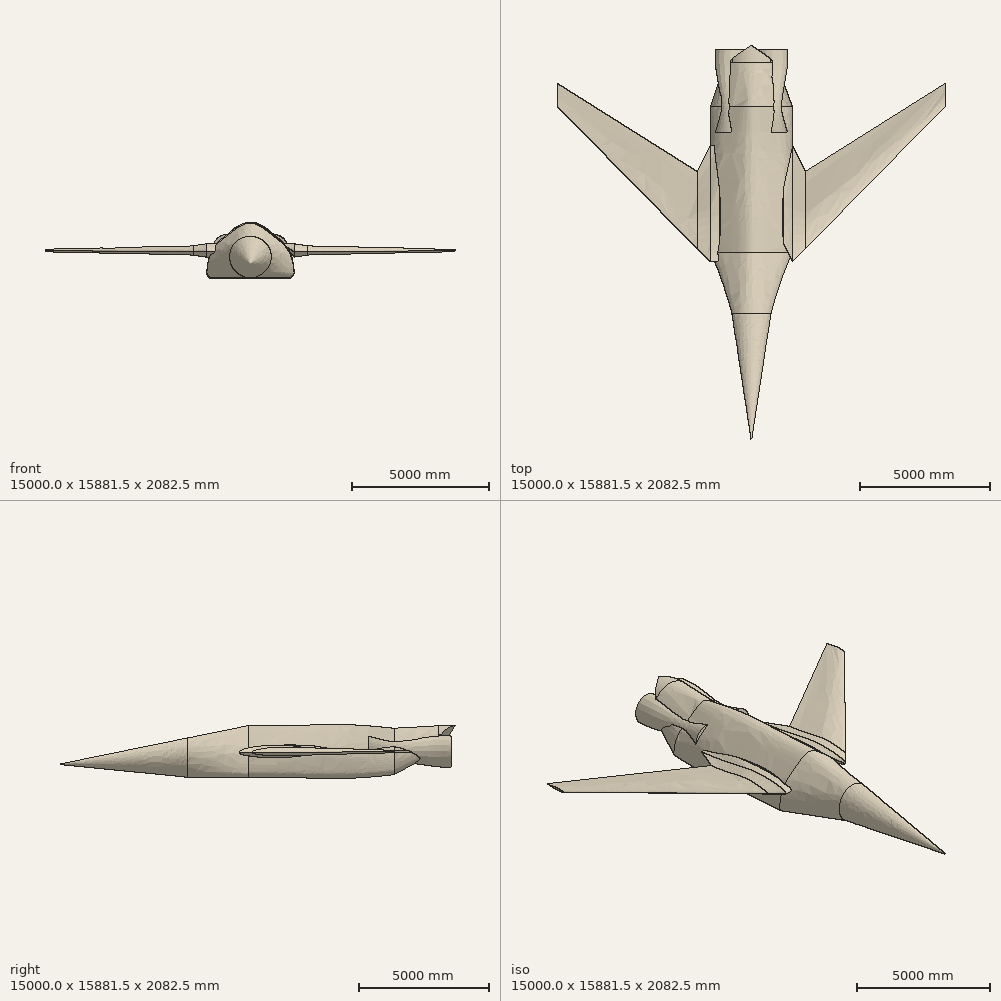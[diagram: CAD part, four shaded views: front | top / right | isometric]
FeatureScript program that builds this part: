
annotation { "Feature Type Name" : "Feature", "Feature Type Description" : "" }
export const myFeature = defineFeature(function(context is Context, id is Id, definition is map)
    precondition{}
    {
        {
            var Q0;
            Q0=qCreatedBy(makeId("Right.planeOp"),FACE);
            var sketch = newSketch(context, id + "F0", { "sketchPlane" : qUnion([Q0])});
            skLineSegment(sketch, "E0", {"start": v(0, 0) * mm, "end": v(-1750, 0) * mm});
            skLineSegment(sketch, "E1", {"start": v(-1750, 0) * mm, "end": v(-3500, 0) * mm});
            skLineSegment(sketch, "E2", {"start": v(-3500, 0) * mm, "end": v(-3500, -1000) * mm});
            skLineSegment(sketch, "E3", {"start": v(-3500, -1000) * mm, "end": v(-8500, -1000) * mm});
            skLineSegment(sketch, "E4", {"start": v(-8500, -1000) * mm, "end": v(-8500, -499.31) * mm});
            skLineSegment(sketch, "E5", {"start": v(-1151.4, 0) * mm, "end": v(-1151.4, 1000) * mm});
            skLineSegment(sketch, "E6", {"start": v(-1151.4, 1000) * mm, "end": v(-8500, -499.31) * mm});
            skLineSegment(sketch, "E7", {"start": v(-8500, -499.31) * mm, "end": v(-3500, -1000) * mm});
            skLineSegment(sketch, "E8", {"start": v(-3500, 0) * mm, "end": v(-3500, 520.82) * mm});
            skLineSegment(sketch, "E9", {"start": v(-8500, -499.31) * mm, "end": v(-8450, -499.31) * mm});
            skLineSegment(sketch, "E10", {"start": v(-8450, -499.31) * mm, "end": v(-8450, -489.1) * mm});
            skLineSegment(sketch, "E11", {"start": v(-8450, -499.31) * mm, "end": v(-8450, -504.32) * mm});
            skSolve(sketch);
        }
        {
            var Q0;
            Q0=sQuery(id+"F0.wireOp",EDGE,"E5");
            cPlane(context, id + "F1", {"entities" : qUnion([Q0]), "cplaneType" : CPlaneType.LINE_ANGLE, "offset" : 25 * mm, "angle" : 90 * degree, "oppositeDirection" : true, "width" : 150 * mm, "height" : 150 * mm});
        }
        {
            var Q0;
            Q0=qCreatedBy(id+"F1.planeOp",FACE);
            var sketch = newSketch(context, id + "F2", { "sketchPlane" : qUnion([Q0])});
            skLineSegment(sketch, "E12.top", {"start": v(-1394.2, -1000) * mm, "end": v(1394.2, -1000) * mm});
            skPoint(sketch, "E12.middle", {"position": v(0, 0) * mm});
            skFitSpline(sketch, "E13", {"points": [v(-1600, -1000) * mm, v(-848, 530) * mm, v(0, 1000) * mm, v(848, 530) * mm, v(1600, -1000) * mm], "startDerivative": vector(0, 10524.75) * mm, "endDerivative": vector(0, -10524.75) * mm});
            skArc(sketch, "E14", {"start": v(-735.27, 618.52) * mm, "mid": v(-1273.27, 435.52) * mm, "end": v(-1440.68, -107.53) * mm});
            skArc(sketch, "E15", {"start": v(1440.68, -107.53) * mm, "mid": v(1273.27, 435.52) * mm, "end": v(735.27, 618.52) * mm});
            skFitSpline(sketch, "E16.trimOffspring", {"points": [v(-1600, -1000) * mm, v(-848, 530) * mm, v(0, 1000) * mm, v(848, 530) * mm, v(1600, -1000) * mm], "startDerivative": vector(0, 10524.75) * mm, "endDerivative": vector(0, -10524.75) * mm});
            skFitSpline(sketch, "E17.trimOffspring", {"points": [v(-1600, -1000) * mm, v(-848, 530) * mm, v(0, 1000) * mm, v(848, 530) * mm, v(1600, -1000) * mm], "startDerivative": vector(0, 10524.75) * mm, "endDerivative": vector(0, -10524.75) * mm});
            skArc(sketch, "E18.filletArc", {"start": v(-1593.82, -787.83) * mm, "mid": v(-1539.85, -937.05) * mm, "end": v(-1394.2, -1000) * mm});
            skArc(sketch, "E19.filletArc", {"start": v(1394.2, -1000) * mm, "mid": v(1539.85, -937.05) * mm, "end": v(1593.82, -787.83) * mm});
            skSolve(sketch);
        }
        {
            var Q0;
            Q0=qCreatedBy(makeId("Front.planeOp"),FACE);
            var sketch = newSketch(context, id + "F3", { "sketchPlane" : qUnion([Q0])});
            skLineSegment(sketch, "E20.top", {"start": v(-1394.2, -1000) * mm, "end": v(1394.2, -1000) * mm});
            skPoint(sketch, "E20.middle", {"position": v(0, 0) * mm});
            skFitSpline(sketch, "E21", {"points": [v(-1600, -1000) * mm, v(-848, 530) * mm, v(0, 1000) * mm, v(848, 530) * mm, v(1600, -1000) * mm], "startDerivative": vector(0, 10524.75) * mm, "endDerivative": vector(0, -10524.75) * mm});
            skArc(sketch, "E22", {"start": v(-735.27, 618.52) * mm, "mid": v(-1273.27, 435.52) * mm, "end": v(-1440.68, -107.53) * mm});
            skArc(sketch, "E23", {"start": v(1440.68, -107.53) * mm, "mid": v(1273.27, 435.52) * mm, "end": v(735.27, 618.52) * mm});
            skFitSpline(sketch, "E24.trimOffspring", {"points": [v(-1600, -1000) * mm, v(-848, 530) * mm, v(0, 1000) * mm, v(848, 530) * mm, v(1600, -1000) * mm], "startDerivative": vector(0, 10524.75) * mm, "endDerivative": vector(0, -10524.75) * mm});
            skFitSpline(sketch, "E25.trimOffspring", {"points": [v(-1600, -1000) * mm, v(-848, 530) * mm, v(0, 1000) * mm, v(848, 530) * mm, v(1600, -1000) * mm], "startDerivative": vector(0, 10524.75) * mm, "endDerivative": vector(0, -10524.75) * mm});
            skArc(sketch, "E26.filletArc", {"start": v(-1593.82, -787.83) * mm, "mid": v(-1539.85, -937.05) * mm, "end": v(-1394.2, -1000) * mm});
            skArc(sketch, "E27.filletArc", {"start": v(1394.2, -1000) * mm, "mid": v(1539.85, -937.05) * mm, "end": v(1593.82, -787.83) * mm});
            skSolve(sketch);
        }
        {
            var Q0;
            Q0=qCreatedBy(makeId("Front.planeOp"),FACE);
            cPlane(context, id + "F4", {"entities" : qUnion([Q0]), "cplaneType" : CPlaneType.OFFSET, "offset" : 3500 * mm, "oppositeDirection" : true, "width" : 150 * mm, "height" : 150 * mm});
        }
        {
            var Q0;
            Q0=qCreatedBy(id+"F4.planeOp",FACE);
            var sketch = newSketch(context, id + "F5", { "sketchPlane" : qUnion([Q0])});
            skLineSegment(sketch, "E28.top", {"start": v(-1394.2, -1000) * mm, "end": v(1394.2, -1000) * mm});
            skPoint(sketch, "E28.middle", {"position": v(0, 0) * mm});
            skFitSpline(sketch, "E29", {"points": [v(-1600, -1000) * mm, v(-848, 530) * mm, v(0, 1000) * mm, v(848, 530) * mm, v(1600, -1000) * mm], "startDerivative": vector(0, 10524.75) * mm, "endDerivative": vector(0, -10524.75) * mm});
            skArc(sketch, "E30", {"start": v(-735.27, 618.52) * mm, "mid": v(-1273.27, 435.52) * mm, "end": v(-1440.68, -107.53) * mm});
            skArc(sketch, "E31", {"start": v(1440.68, -107.53) * mm, "mid": v(1273.27, 435.52) * mm, "end": v(735.27, 618.52) * mm});
            skFitSpline(sketch, "E32.trimOffspring", {"points": [v(-1600, -1000) * mm, v(-848, 530) * mm, v(0, 1000) * mm, v(848, 530) * mm, v(1600, -1000) * mm], "startDerivative": vector(0, 10524.75) * mm, "endDerivative": vector(0, -10524.75) * mm});
            skFitSpline(sketch, "E33.trimOffspring", {"points": [v(-1600, -1000) * mm, v(-848, 530) * mm, v(0, 1000) * mm, v(848, 530) * mm, v(1600, -1000) * mm], "startDerivative": vector(0, 10524.75) * mm, "endDerivative": vector(0, -10524.75) * mm});
            skArc(sketch, "E34.filletArc", {"start": v(-1593.82, -787.83) * mm, "mid": v(-1539.85, -937.05) * mm, "end": v(-1394.2, -1000) * mm});
            skArc(sketch, "E35.filletArc", {"start": v(1394.2, -1000) * mm, "mid": v(1539.85, -937.05) * mm, "end": v(1593.82, -787.83) * mm});
            skSolve(sketch);
        }
        {
            var Q0;
            Q0=qCreatedBy(makeId("Front.planeOp"),FACE);
            cPlane(context, id + "F6", {"entities" : qUnion([Q0]), "cplaneType" : CPlaneType.OFFSET, "offset" : 4500 * mm, "oppositeDirection" : true, "width" : 150 * mm, "height" : 150 * mm});
        }
        {
            var Q0;
            Q0=qCreatedBy(id+"F6.planeOp",FACE);
            var sketch = newSketch(context, id + "F7", { "sketchPlane" : qUnion([Q0])});
            skLineSegment(sketch, "E36.top", {"start": v(-1413.07, -900) * mm, "end": v(1413.07, -900) * mm});
            skPoint(sketch, "E36.middle", {"position": v(0, 0) * mm});
            skFitSpline(sketch, "E37", {"points": [v(-1600, -900) * mm, v(-784.42, 441.24) * mm, v(0, 900) * mm, v(784.42, 441.24) * mm, v(1600, -900) * mm], "startDerivative": vector(0, 9508.62) * mm, "endDerivative": vector(0, -9508.62) * mm});
            skArc(sketch, "E38", {"start": v(-719.25, 488.69) * mm, "mid": v(-1131.76, 394.84) * mm, "end": v(-1324.66, 18.33) * mm});
            skArc(sketch, "E39", {"start": v(1324.66, 18.33) * mm, "mid": v(1131.76, 394.84) * mm, "end": v(719.25, 488.69) * mm});
            skFitSpline(sketch, "E40.trimOffspring", {"points": [v(-1600, -900) * mm, v(-784.42, 441.24) * mm, v(0, 900) * mm, v(784.42, 441.24) * mm, v(1600, -900) * mm], "startDerivative": vector(0, 9508.62) * mm, "endDerivative": vector(0, -9508.62) * mm});
            skFitSpline(sketch, "E41.trimOffspring", {"points": [v(-1600, -900) * mm, v(-784.42, 441.24) * mm, v(0, 900) * mm, v(784.42, 441.24) * mm, v(1600, -900) * mm], "startDerivative": vector(0, 9508.62) * mm, "endDerivative": vector(0, -9508.62) * mm});
            skArc(sketch, "E42.filletArc", {"start": v(-1592.48, -705.43) * mm, "mid": v(-1545.4, -842.02) * mm, "end": v(-1413.07, -900) * mm});
            skArc(sketch, "E43.filletArc", {"start": v(1413.07, -900) * mm, "mid": v(1545.4, -842.02) * mm, "end": v(1592.48, -705.43) * mm});
            skLineSegment(sketch, "E44", {"start": v(-719.25, 488.69) * mm, "end": v(-1324.66, 18.33) * mm, "construction": true});
            skLineSegment(sketch, "E45", {"start": v(719.25, 488.69) * mm, "end": v(1324.66, 18.33) * mm, "construction": true});
            skSolve(sketch);
        }
        {
            var Q0;
            Q0=qCreatedBy(makeId("Front.planeOp"),FACE);
            cPlane(context, id + "F8", {"entities" : qUnion([Q0]), "cplaneType" : CPlaneType.OFFSET, "offset" : 6232.05 * mm, "oppositeDirection" : true, "width" : 150 * mm, "height" : 150 * mm});
        }
        {
            var Q0;
            Q0=qCreatedBy(id+"F8.planeOp",FACE);
            var sketch = newSketch(context, id + "F9", { "sketchPlane" : qUnion([Q0])});
            skArc(sketch, "E46", {"start": v(998.61, 52.63) * mm, "mid": v(0, 1000) * mm, "end": v(-998.61, 52.63) * mm});
            skLineSegment(sketch, "E47", {"start": v(0, 0) * mm, "end": v(-948.68, 0) * mm});
            skLineSegment(sketch, "E48", {"start": v(0, 0) * mm, "end": v(948.68, 0) * mm});
            skLineSegment(sketch, "E49", {"start": v(0, 1000) * mm, "end": v(0, 675) * mm, "construction": true});
            skLineSegment(sketch, "E50", {"start": v(0, 675) * mm, "end": v(-737.82, 675) * mm, "construction": true});
            skLineSegment(sketch, "E51", {"start": v(0, 675) * mm, "end": v(737.82, 675) * mm, "construction": true});
            skPoint(sketch, "E52.visualSharp", {"position": v(-1000, 0) * mm});
            skArc(sketch, "E52.filletArc", {"start": v(-998.61, 52.63) * mm, "mid": v(-984.96, 15.59) * mm, "end": v(-948.68, 0) * mm});
            skPoint(sketch, "E53.visualSharp", {"position": v(1000, 0) * mm});
            skArc(sketch, "E53.filletArc", {"start": v(948.68, 0) * mm, "mid": v(984.96, 15.59) * mm, "end": v(998.61, 52.63) * mm});
            skSolve(sketch);
        }
        {
            var Q0;
            Q0=makeQuery(id+"F2.imprint","IMPRINT",FACE,{"disambiguationData":[TD([[makeQuery(id+"F2.imprint","IMPRINT",EDGE,{"derivedFrom":sQuery(id+"F2.wireOp",EDGE,"E12.top")}),1.0]])]});
            var Q1;
            Q1=makeQuery(id+"F3.imprint","IMPRINT",FACE,{"disambiguationData":[TD([[makeQuery(id+"F3.imprint","IMPRINT",EDGE,{"derivedFrom":sQuery(id+"F3.wireOp",EDGE,"E20.top")}),1.0]])]});
            var Q2;
            Q2=makeQuery(id+"F5.imprint","IMPRINT",FACE,{"disambiguationData":[TD([[makeQuery(id+"F5.imprint","IMPRINT",EDGE,{"derivedFrom":sQuery(id+"F5.wireOp",EDGE,"E28.top")}),1.0]])]});
            var Q3;
            Q3=makeQuery(id+"F7.imprint","IMPRINT",FACE,{"disambiguationData":[TD([[makeQuery(id+"F7.imprint","IMPRINT",EDGE,{"derivedFrom":sQuery(id+"F7.wireOp",EDGE,"E36.top")}),1.0]])]});
            loft(context, id + "F10", {"sheetProfilesArray" : [{ "sheetProfileEntities" : qUnion([Q0]) }, { "sheetProfileEntities" : qUnion([Q1]) }, { "sheetProfileEntities" : qUnion([Q2]) }, { "sheetProfileEntities" : qUnion([Q3]) }]});
        }
        {
            var Q0;
            Q0=sQuery(id+"F7.wireOp",EDGE,"E44");
            var Q1;
            Q1=sQuery(id+"F9.wireOp",VERTEX,"E50.end");
            cPlane(context, id + "F11", {"entities" : qUnion([Q0, Q1]), "cplaneType" : CPlaneType.LINE_ANGLE, "offset" : 25 * mm, "angle" : 180 * degree, "width" : 150 * mm, "height" : 150 * mm});
        }
        {
            var Q0;
            Q0=qCreatedBy(id+"F11.planeOp",FACE);
            var sketch = newSketch(context, id + "F12", { "sketchPlane" : qUnion([Q0])});
            skLineSegment(sketch, "E54", {"start": v(-589.34, 4526.34) * mm, "end": v(-612.8, 6268.32) * mm});
            skLineSegment(sketch, "E55", {"start": v(-1354.08, 4472.19) * mm, "end": v(-612.8, 6268.32) * mm});
            skSolve(sketch);
        }
        {
            var Q0;
            Q0=sQuery(id+"F7.wireOp",EDGE,"E45");
            var Q1;
            Q1=sQuery(id+"F9.wireOp",VERTEX,"E51.end");
            cPlane(context, id + "F13", {"entities" : qUnion([Q0, Q1]), "cplaneType" : CPlaneType.LINE_ANGLE, "offset" : 25 * mm, "angle" : 0 * degree, "width" : 150 * mm, "height" : 150 * mm});
        }
        {
            var Q0;
            Q0=qCreatedBy(id+"F13.planeOp",FACE);
            var sketch = newSketch(context, id + "F14", { "sketchPlane" : qUnion([Q0])});
            skLineSegment(sketch, "E56", {"start": v(589.34, 4526.34) * mm, "end": v(612.8, 6268.32) * mm});
            skLineSegment(sketch, "E57", {"start": v(1354.08, 4472.19) * mm, "end": v(612.8, 6268.32) * mm});
            skSolve(sketch);
        }
        {
            var Q1;
            Q1=makeQuery(id+"F10.opLoft","CAP_FACE",FACE,{"disambiguationData":[OSD([makeQuery(id+"F7.imprint","IMPRINT",FACE,{"disambiguationData":[TD([[makeQuery(id+"F7.imprint","IMPRINT",EDGE,{"derivedFrom":sQuery(id+"F7.wireOp",EDGE,"E36.top")}),1.0]])]})])],"isStart":true});
            var Q2;
            Q2=makeQuery(id+"F9.imprint","IMPRINT",FACE,{"disambiguationData":[TD([[makeQuery(id+"F9.imprint","IMPRINT",EDGE,{"derivedFrom":sQuery(id+"F9.wireOp",EDGE,"E46")}),1.0]])]});
            var Q3;
            Q3=sQuery(id+"F12.wireOp",EDGE,"E54");
            var Q4;
            Q4=sQuery(id+"F14.wireOp",EDGE,"E56");
            loft(context, id + "F15", {"operationType" : NewBodyOperationType.ADD, "addGuides" : true, "sheetProfilesArray" : [{ "sheetProfileEntities" : qUnion([Q1]) }, { "sheetProfileEntities" : qUnion([Q2]) }], "guidesArray" : [{ "guideEntities" : qUnion([Q3]), "guideDerivativeType" : LoftGuideDerivativeType.DEFAULT, "guideDerivativeMagnitude" : 1 }, { "guideEntities" : qUnion([Q4]), "guideDerivativeType" : LoftGuideDerivativeType.DEFAULT, "guideDerivativeMagnitude" : 1 }]});
        }
        {
            var Q0;
            Q0=makeQuery(id+"F15.opLoft","CAP_FACE",FACE,{"disambiguationData":[OSD([makeQuery(id+"F9.imprint","IMPRINT",FACE,{"disambiguationData":[TD([[makeQuery(id+"F9.imprint","IMPRINT",EDGE,{"derivedFrom":sQuery(id+"F9.wireOp",EDGE,"E46")}),1.0]])]})])],"isStart":true});
            extrude(context, id + "F16", {"entities" : qUnion([Q0]), "operationType" : NewBodyOperationType.ADD, "depth" : 649.4 * mm, "offsetDistance" : 25 * mm});
        }
        {
            var Q0;
            Q0=qCreatedBy(makeId("Right.planeOp"),FACE);
            var sketch = newSketch(context, id + "F17", { "sketchPlane" : qUnion([Q0])});
            skLineSegment(sketch, "E58", {"start": v(0, 0) * mm, "end": v(4500, 0) * mm});
            skLineSegment(sketch, "E59", {"start": v(4500, 0) * mm, "end": v(6232.05, 0) * mm});
            skLineSegment(sketch, "E60", {"start": v(4500, 0) * mm, "end": v(4500, 1000) * mm});
            skLineSegment(sketch, "E61", {"start": v(4500, 1000) * mm, "end": v(6881.46, 1000) * mm});
            skLineSegment(sketch, "E62", {"start": v(6881.46, 1000) * mm, "end": v(6881.46, -1000) * mm});
            skLineSegment(sketch, "E63", {"start": v(6881.46, 1000) * mm, "end": v(6232.05, 0) * mm});
            skLineSegment(sketch, "E64", {"start": v(6232.05, 0) * mm, "end": v(5582.64, -1000) * mm});
            skLineSegment(sketch, "E65", {"start": v(5582.64, -1000) * mm, "end": v(6881.46, -1000) * mm});
            skSolve(sketch);
        }
        {
            var Q0;
            Q0=makeQuery(id+"F17.imprint","IMPRINT",FACE,{"disambiguationData":[TD([[makeQuery(id+"F17.imprint","IMPRINT",EDGE,{"derivedFrom":sQuery(id+"F17.wireOp",EDGE,"E62")}),-1.0]])]});
            var Q1;
            Q1=sQuery(id+"F17.wireOp",EDGE,"E61");
            revolve(context, id + "F18", {"operationType" : NewBodyOperationType.REMOVE, "entities" : qUnion([Q0]), "axis" : qUnion([Q1]), "revolveType" : RevolveType.SYMMETRIC, "oppositeDirection" : true, "angle" : 182 * degree});
        }
        {
            var Q0;
            Q0=qCreatedBy(id+"F1.planeOp",FACE);
            var sketch = newSketch(context, id + "F19", { "sketchPlane" : qUnion([Q0])});
            skLineSegment(sketch, "E66.top", {"start": v(-1394.2, -1000) * mm, "end": v(1394.2, -1000) * mm});
            skPoint(sketch, "E66.middle", {"position": v(0, 0) * mm});
            skFitSpline(sketch, "E67", {"points": [v(-1600, -1000) * mm, v(-848, 530) * mm, v(0, 1000) * mm, v(848, 530) * mm, v(1600, -1000) * mm], "startDerivative": vector(0, 10524.75) * mm, "endDerivative": vector(0, -10524.75) * mm});
            skArc(sketch, "E68.filletArc", {"start": v(-1593.82, -787.83) * mm, "mid": v(-1539.85, -937.05) * mm, "end": v(-1394.2, -1000) * mm});
            skArc(sketch, "E69.filletArc", {"start": v(1394.2, -1000) * mm, "mid": v(1539.85, -937.05) * mm, "end": v(1593.82, -787.83) * mm});
            skLineSegment(sketch, "E70", {"start": v(-1593.82, -787.83) * mm, "end": v(-1394.2, -1000) * mm, "construction": true});
            skLineSegment(sketch, "E71", {"start": v(1593.82, -787.83) * mm, "end": v(1394.2, -1000) * mm, "construction": true});
            skSolve(sketch);
        }
        {
            var Q0;
            Q0=qCreatedBy(makeId("Front.planeOp"),FACE);
            cPlane(context, id + "F20", {"entities" : qUnion([Q0]), "cplaneType" : CPlaneType.OFFSET, "offset" : 3500 * mm, "width" : 150 * mm, "height" : 150 * mm});
        }
        {
            var Q0;
            Q0=qCreatedBy(id+"F20.planeOp",FACE);
            var sketch = newSketch(context, id + "F21", { "sketchPlane" : qUnion([Q0])});
            skCircle(sketch, "E72", {"center": v(0, -239.59) * mm, "radius": 760.41 * mm});
            skLineSegment(sketch, "E73", {"start": v(0, -1000) * mm, "end": v(0, -800) * mm, "construction": true});
            skLineSegment(sketch, "E74", {"start": v(0, -800) * mm, "end": v(-513.97, -800) * mm, "construction": true});
            skLineSegment(sketch, "E75", {"start": v(0, -800) * mm, "end": v(513.97, -800) * mm, "construction": true});
            skSolve(sketch);
        }
        {
            var Q0;
            Q0=qCreatedBy(makeId("Front.planeOp"),FACE);
            cPlane(context, id + "F22", {"entities" : qUnion([Q0]), "cplaneType" : CPlaneType.OFFSET, "offset" : 8450 * mm, "width" : 150 * mm, "height" : 150 * mm});
        }
        {
            var Q0;
            Q0=qCreatedBy(id+"F22.planeOp",FACE);
            var sketch = newSketch(context, id + "F23", { "sketchPlane" : qUnion([Q0])});
            skCircle(sketch, "E76", {"center": v(0, -496.71) * mm, "radius": 7.6 * mm});
            skSolve(sketch);
        }
        {
            var Q0;
            Q0=sQuery(id+"F19.wireOp",EDGE,"E70");
            var Q1;
            Q1=sQuery(id+"F21.wireOp",VERTEX,"E74.end");
            cPlane(context, id + "F24", {"entities" : qUnion([Q0, Q1]), "cplaneType" : CPlaneType.LINE_ANGLE, "offset" : 25 * mm, "angle" : 0 * degree, "width" : 150 * mm, "height" : 150 * mm});
        }
        {
            var Q0;
            Q0=qCreatedBy(id+"F24.planeOp",FACE);
            var sketch = newSketch(context, id + "F25", { "sketchPlane" : qUnion([Q0])});
            skLineSegment(sketch, "E77", {"start": v(3032.27, -230.44) * mm, "end": v(558.11, 518.4) * mm});
            skLineSegment(sketch, "E78", {"start": v(3032.27, -230.44) * mm, "end": v(558.11, 227.09) * mm});
            skSolve(sketch);
        }
        {
            var Q0;
            Q0=sQuery(id+"F19.wireOp",EDGE,"E71");
            var Q1;
            Q1=sQuery(id+"F21.wireOp",VERTEX,"E75.end");
            cPlane(context, id + "F26", {"entities" : qUnion([Q0, Q1]), "cplaneType" : CPlaneType.LINE_ANGLE, "offset" : 25 * mm, "angle" : 180 * degree, "width" : 150 * mm, "height" : 150 * mm});
        }
        {
            var Q0;
            Q0=qCreatedBy(id+"F26.planeOp",FACE);
            var sketch = newSketch(context, id + "F27", { "sketchPlane" : qUnion([Q0])});
            skLineSegment(sketch, "E79", {"start": v(-3032.27, -230.44) * mm, "end": v(-558.11, 518.4) * mm});
            skLineSegment(sketch, "E80", {"start": v(-3032.27, -230.44) * mm, "end": v(-558.11, 227.09) * mm});
            skSolve(sketch);
        }
        {
            var Q1;
            Q1=makeQuery(id+"F19.imprint","IMPRINT",FACE,{"disambiguationData":[TD([[makeQuery(id+"F19.imprint","IMPRINT",EDGE,{"derivedFrom":sQuery(id+"F19.wireOp",EDGE,"E66.top")}),1.0]])]});
            var Q2;
            Q2=makeQuery(id+"F21.imprint","IMPRINT",FACE,{"disambiguationData":[TD([[makeQuery(id+"F21.imprint","IMPRINT",EDGE,{"derivedFrom":sQuery(id+"F21.wireOp",EDGE,"E72")}),1.0]])]});
            var Q3;
            Q3=sQuery(id+"F25.wireOp",EDGE,"E77");
            var Q4;
            Q4=sQuery(id+"F27.wireOp",EDGE,"E79");
            loft(context, id + "F28", {"operationType" : NewBodyOperationType.ADD, "addGuides" : true, "sheetProfilesArray" : [{ "sheetProfileEntities" : qUnion([Q1]) }, { "sheetProfileEntities" : qUnion([Q2]) }], "guidesArray" : [{ "guideEntities" : qUnion([Q3]), "guideDerivativeType" : LoftGuideDerivativeType.DEFAULT, "guideDerivativeMagnitude" : 1 }, { "guideEntities" : qUnion([Q4]), "guideDerivativeType" : LoftGuideDerivativeType.DEFAULT, "guideDerivativeMagnitude" : 1 }]});
        }
        {
            var Q1;
            Q1=makeQuery(id+"F28.opLoft","CAP_FACE",FACE,{"disambiguationData":[OSD([makeQuery(id+"F21.imprint","IMPRINT",FACE,{"disambiguationData":[TD([[makeQuery(id+"F21.imprint","IMPRINT",EDGE,{"derivedFrom":sQuery(id+"F21.wireOp",EDGE,"E72")}),1.0]])]})])],"isStart":true});
            var Q2;
            Q2=makeQuery(id+"F23.imprint","IMPRINT",FACE,{"disambiguationData":[TD([[makeQuery(id+"F23.imprint","IMPRINT",EDGE,{"derivedFrom":sQuery(id+"F23.wireOp",EDGE,"E76")}),1.0]])]});
            loft(context, id + "F29", {"operationType" : NewBodyOperationType.ADD, "sheetProfilesArray" : [{ "sheetProfileEntities" : qUnion([Q1]) }, { "sheetProfileEntities" : qUnion([Q2]) }]});
        }
        {
            var Q0;
            Q0=makeQuery(id+"F29.opLoft","CAP_FACE",FACE,{"disambiguationData":[OSD([makeQuery(id+"F23.imprint","IMPRINT",FACE,{"disambiguationData":[TD([[makeQuery(id+"F23.imprint","IMPRINT",EDGE,{"derivedFrom":sQuery(id+"F23.wireOp",EDGE,"E76")}),1.0]])]})])],"isStart":true});
            extrude(context, id + "F30", {"entities" : qUnion([Q0]), "operationType" : NewBodyOperationType.ADD, "depth" : 550 * mm, "offsetDistance" : 25 * mm});
        }
        {
            var Q0;
            Q0=qCreatedBy(makeId("Front.planeOp"),FACE);
            cPlane(context, id + "F31", {"entities" : qUnion([Q0]), "cplaneType" : CPlaneType.OFFSET, "offset" : 3500 * mm, "oppositeDirection" : true, "width" : 150 * mm, "height" : 150 * mm});
        }
        {
            var Q0;
            Q0=qCreatedBy(id+"F31.planeOp",FACE);
            var sketch = newSketch(context, id + "F32", { "sketchPlane" : qUnion([Q0])});
            skCircle(sketch, "E81", {"center": v(-800, 0) * mm, "radius": 600 * mm});
            skCircle(sketch, "E82", {"center": v(800, 0) * mm, "radius": 600 * mm});
            skSolve(sketch);
        }
        {
            var Q0;
            Q0=qCreatedBy(makeId("Front.planeOp"),FACE);
            cPlane(context, id + "F33", {"entities" : qUnion([Q0]), "cplaneType" : CPlaneType.OFFSET, "offset" : 4500 * mm, "oppositeDirection" : true, "width" : 150 * mm, "height" : 150 * mm});
        }
        {
            var Q0;
            Q0=qCreatedBy(id+"F33.planeOp",FACE);
            var sketch = newSketch(context, id + "F34", { "sketchPlane" : qUnion([Q0])});
            skCircle(sketch, "E83", {"center": v(-800, 0) * mm, "radius": 400 * mm});
            skCircle(sketch, "E84", {"center": v(800, 0) * mm, "radius": 400 * mm});
            skSolve(sketch);
        }
        {
            var Q0;
            Q0=qCreatedBy(makeId("Front.planeOp"),FACE);
            cPlane(context, id + "F35", {"entities" : qUnion([Q0]), "cplaneType" : CPlaneType.OFFSET, "offset" : 6232.05 * mm, "oppositeDirection" : true, "width" : 150 * mm, "height" : 150 * mm});
        }
        {
            var Q0;
            Q0=qCreatedBy(id+"F35.planeOp",FACE);
            var sketch = newSketch(context, id + "F36", { "sketchPlane" : qUnion([Q0])});
            skCircle(sketch, "E85", {"center": v(-800, 0) * mm, "radius": 600 * mm});
            skCircle(sketch, "E86", {"center": v(800, 0) * mm, "radius": 600 * mm});
            skSolve(sketch);
        }
        {
            var Q0;
            Q0=qCreatedBy(makeId("Front.planeOp"),FACE);
            cPlane(context, id + "F37", {"entities" : qUnion([Q0]), "cplaneType" : CPlaneType.OFFSET, "offset" : 6732.05 * mm, "oppositeDirection" : true, "width" : 150 * mm, "height" : 150 * mm});
        }
        {
            var Q0;
            Q0=qCreatedBy(id+"F37.planeOp",FACE);
            var sketch = newSketch(context, id + "F38", { "sketchPlane" : qUnion([Q0])});
            skCircle(sketch, "E87", {"center": v(-800, 0) * mm, "radius": 600 * mm});
            skCircle(sketch, "E88", {"center": v(800, 0) * mm, "radius": 600 * mm});
            skSolve(sketch);
        }
        {
            var Q0;
            Q0=makeQuery(id+"F32.imprint","IMPRINT",FACE,{"disambiguationData":[TD([[makeQuery(id+"F32.imprint","IMPRINT",EDGE,{"derivedFrom":sQuery(id+"F32.wireOp",EDGE,"E81")}),1.0]])]});
            var Q1;
            Q1=makeQuery(id+"F34.imprint","IMPRINT",FACE,{"disambiguationData":[TD([[makeQuery(id+"F34.imprint","IMPRINT",EDGE,{"derivedFrom":sQuery(id+"F34.wireOp",EDGE,"E83")}),1.0]])]});
            var Q2;
            Q2=makeQuery(id+"F36.imprint","IMPRINT",FACE,{"disambiguationData":[TD([[makeQuery(id+"F36.imprint","IMPRINT",EDGE,{"derivedFrom":sQuery(id+"F36.wireOp",EDGE,"E85")}),1.0]])]});
            var Q3;
            Q3=makeQuery(id+"F38.imprint","IMPRINT",FACE,{"disambiguationData":[TD([[makeQuery(id+"F38.imprint","IMPRINT",EDGE,{"derivedFrom":sQuery(id+"F38.wireOp",EDGE,"E87")}),1.0]])]});
            loft(context, id + "F39", {"sheetProfilesArray" : [{ "sheetProfileEntities" : qUnion([Q0]) }, { "sheetProfileEntities" : qUnion([Q1]) }, { "sheetProfileEntities" : qUnion([Q2]) }, { "sheetProfileEntities" : qUnion([Q3]) }]});
        }
        {
            var Q0;
            Q0=makeQuery(id+"F32.imprint","IMPRINT",FACE,{"disambiguationData":[TD([[makeQuery(id+"F32.imprint","IMPRINT",EDGE,{"derivedFrom":sQuery(id+"F32.wireOp",EDGE,"E82")}),1.0]])]});
            var Q1;
            Q1=makeQuery(id+"F34.imprint","IMPRINT",FACE,{"disambiguationData":[TD([[makeQuery(id+"F34.imprint","IMPRINT",EDGE,{"derivedFrom":sQuery(id+"F34.wireOp",EDGE,"E84")}),1.0]])]});
            var Q2;
            Q2=makeQuery(id+"F36.imprint","IMPRINT",FACE,{"disambiguationData":[TD([[makeQuery(id+"F36.imprint","IMPRINT",EDGE,{"derivedFrom":sQuery(id+"F36.wireOp",EDGE,"E86")}),1.0]])]});
            var Q3;
            Q3=makeQuery(id+"F38.imprint","IMPRINT",FACE,{"disambiguationData":[TD([[makeQuery(id+"F38.imprint","IMPRINT",EDGE,{"derivedFrom":sQuery(id+"F38.wireOp",EDGE,"E88")}),1.0]])]});
            loft(context, id + "F40", {"sheetProfilesArray" : [{ "sheetProfileEntities" : qUnion([Q0]) }, { "sheetProfileEntities" : qUnion([Q1]) }, { "sheetProfileEntities" : qUnion([Q2]) }, { "sheetProfileEntities" : qUnion([Q3]) }]});
        }
        {
            var Q0;
            Q0=qCreatedBy(makeId("Right.planeOp"),FACE);
            var sketch = newSketch(context, id + "F41", { "sketchPlane" : qUnion([Q0])});
            skFitSpline(sketch, "E89", {"points": [v(-1500, -50) * mm, v(0, 250) * mm, v(3000, -50) * mm, v(0, -250) * mm, v(-1500, -50) * mm]});
            skSolve(sketch);
        }
        {
            var Q0;
            Q0=qCreatedBy(makeId("Right.planeOp"),FACE);
            cPlane(context, id + "F42", {"entities" : qUnion([Q0]), "cplaneType" : CPlaneType.OFFSET, "offset" : 1600 * mm, "oppositeDirection" : true, "width" : 150 * mm, "height" : 150 * mm});
        }
        {
            var Q0;
            Q0=qCreatedBy(id+"F42.planeOp",FACE);
            var sketch = newSketch(context, id + "F43", { "sketchPlane" : qUnion([Q0])});
            skFitSpline(sketch, "E90", {"points": [v(-1500, -50) * mm, v(0, 250) * mm, v(3000, -50) * mm], "startDerivative": vector(0, 1247.63) * mm, "endDerivative": vector(7705.35, -256.85) * mm});
            skFitSpline(sketch, "E91", {"points": [v(-1500, -50) * mm, v(0, -250) * mm, v(3000, -50) * mm], "startDerivative": vector(0, -722.87) * mm, "endDerivative": vector(7692.49, -256.42) * mm});
            skSolve(sketch);
        }
        {
            var Q0;
            Q0=qCreatedBy(makeId("Right.planeOp"),FACE);
            cPlane(context, id + "F44", {"entities" : qUnion([Q0]), "cplaneType" : CPlaneType.OFFSET, "offset" : 1600 * mm, "width" : 150 * mm, "height" : 150 * mm});
        }
        {
            var Q0;
            Q0=qCreatedBy(id+"F44.planeOp",FACE);
            var sketch = newSketch(context, id + "F45", { "sketchPlane" : qUnion([Q0])});
            skFitSpline(sketch, "E92", {"points": [v(-1500, -50) * mm, v(0, 250) * mm, v(3000, -50) * mm], "startDerivative": vector(0, 1247.63) * mm, "endDerivative": vector(7705.35, -256.85) * mm});
            skFitSpline(sketch, "E93", {"points": [v(-1500, -50) * mm, v(0, -250) * mm, v(3000, -50) * mm], "startDerivative": vector(0, -722.87) * mm, "endDerivative": vector(7692.49, -256.42) * mm});
            skSolve(sketch);
        }
        {
            var Q0;
            Q0=qCreatedBy(makeId("Right.planeOp"),FACE);
            cPlane(context, id + "F46", {"entities" : qUnion([Q0]), "cplaneType" : CPlaneType.OFFSET, "offset" : 2100 * mm, "oppositeDirection" : true, "width" : 150 * mm, "height" : 150 * mm});
        }
        {
            var Q0;
            Q0=qCreatedBy(id+"F46.planeOp",FACE);
            var sketch = newSketch(context, id + "F47", { "sketchPlane" : qUnion([Q0])});
            skFitSpline(sketch, "E94", {"points": [v(-1000, -36) * mm, v(0, 170) * mm, v(2000, -36) * mm], "startDerivative": vector(0, 576.8) * mm, "endDerivative": vector(5137.83, -184.96) * mm});
            skFitSpline(sketch, "E95", {"points": [v(-1000, -36) * mm, v(0, -170) * mm, v(2000, -36) * mm], "startDerivative": vector(0, -484.31) * mm, "endDerivative": vector(5128.4, -184.62) * mm});
            skSolve(sketch);
        }
        {
            var Q0;
            Q0=qCreatedBy(makeId("Right.planeOp"),FACE);
            cPlane(context, id + "F48", {"entities" : qUnion([Q0]), "cplaneType" : CPlaneType.OFFSET, "offset" : 2100 * mm, "width" : 150 * mm, "height" : 150 * mm});
        }
        {
            var Q0;
            Q0=qCreatedBy(id+"F48.planeOp",FACE);
            var sketch = newSketch(context, id + "F49", { "sketchPlane" : qUnion([Q0])});
            skFitSpline(sketch, "E96", {"points": [v(-1000, -36) * mm, v(0, 170) * mm, v(2000, -36) * mm], "startDerivative": vector(0, 576.8) * mm, "endDerivative": vector(5137.83, -184.96) * mm});
            skFitSpline(sketch, "E97", {"points": [v(-1000, -36) * mm, v(0, -170) * mm, v(2000, -36) * mm], "startDerivative": vector(0, -484.31) * mm, "endDerivative": vector(5128.4, -184.62) * mm});
            skSolve(sketch);
        }
        {
            var Q0;
            Q0=qCreatedBy(makeId("Right.planeOp"),FACE);
            cPlane(context, id + "F50", {"entities" : qUnion([Q0]), "cplaneType" : CPlaneType.OFFSET, "offset" : 7500 * mm, "oppositeDirection" : true, "width" : 150 * mm, "height" : 150 * mm});
        }
        {
            var Q0;
            Q0=qCreatedBy(id+"F50.planeOp",FACE);
            var sketch = newSketch(context, id + "F51", { "sketchPlane" : qUnion([Q0])});
            skFitSpline(sketch, "E98", {"points": [v(4500, -10) * mm, v(4800, 50) * mm, v(5400, -10) * mm], "startDerivative": vector(0, 177.4) * mm, "endDerivative": vector(1541.07, -51.37) * mm});
            skFitSpline(sketch, "E99", {"points": [v(4500, -10) * mm, v(4800, -50) * mm, v(5400, -10) * mm], "startDerivative": vector(0, -144.57) * mm, "endDerivative": vector(1538.5, -51.28) * mm});
            skSolve(sketch);
        }
        {
            var Q0;
            Q0=qCreatedBy(makeId("Right.planeOp"),FACE);
            cPlane(context, id + "F52", {"entities" : qUnion([Q0]), "cplaneType" : CPlaneType.OFFSET, "offset" : 7500 * mm, "width" : 150 * mm, "height" : 150 * mm});
        }
        {
            var Q0;
            Q0=qCreatedBy(id+"F52.planeOp",FACE);
            var sketch = newSketch(context, id + "F53", { "sketchPlane" : qUnion([Q0])});
            skFitSpline(sketch, "E100", {"points": [v(4500, -10) * mm, v(4800, 50) * mm, v(5400, -10) * mm], "startDerivative": vector(0, 177.4) * mm, "endDerivative": vector(1541.07, -51.37) * mm});
            skFitSpline(sketch, "E101", {"points": [v(4500, -10) * mm, v(4800, -50) * mm, v(5400, -10) * mm], "startDerivative": vector(0, -144.57) * mm, "endDerivative": vector(1538.5, -51.28) * mm});
            skSolve(sketch);
        }
        {
            var Q0;
            Q0 = qSketchRegion(id + "F41", true);
            extrude(context, id + "F54", {"entities" : qUnion([Q0]), "endBound" : BoundingType.SYMMETRIC, "depth" : 2500 * mm, "offsetDistance" : 25 * mm});
        }
        {
            var Q1;
            Q1=makeQuery(id+"F54.opExtrude","CAP_FACE",FACE,{"disambiguationData":[OSD([sQuery(id+"F41.wireOp",EDGE,"E89")])],"isStart":true});
            var Q2;
            {var subQ0=sQuery(id+"F43.wireOp",EDGE,"E90");Q2=makeQuery(id+"F43.imprint","IMPRINT",FACE,{"disambiguationData":[TD([[makeQuery(id+"F43.imprint","IMPRINT",EDGE,{"derivedFrom":subQ0}),-1.0]])]});}
            loft(context, id + "F55", {"operationType" : NewBodyOperationType.ADD, "sheetProfilesArray" : [{ "sheetProfileEntities" : qUnion([Q1]) }, { "sheetProfileEntities" : qUnion([Q2]) }]});
        }
        {
            var Q1;
            Q1=makeQuery(id+"F54.opExtrude","CAP_FACE",FACE,{"disambiguationData":[OSD([sQuery(id+"F41.wireOp",EDGE,"E89")])],"isStart":false});
            var Q2;
            {var subQ0=sQuery(id+"F45.wireOp",EDGE,"E92");Q2=makeQuery(id+"F45.imprint","IMPRINT",FACE,{"disambiguationData":[TD([[makeQuery(id+"F45.imprint","IMPRINT",EDGE,{"derivedFrom":subQ0}),-1.0]])]});}
            loft(context, id + "F56", {"operationType" : NewBodyOperationType.ADD, "sheetProfilesArray" : [{ "sheetProfileEntities" : qUnion([Q1]) }, { "sheetProfileEntities" : qUnion([Q2]) }]});
        }
        {
            var Q1;
            {var subQ0=sQuery(id+"F43.wireOp",EDGE,"E90");Q1=makeQuery(id+"F55.opLoft","CAP_FACE",FACE,{"disambiguationData":[OSD([makeQuery(id+"F43.imprint","IMPRINT",FACE,{"disambiguationData":[TD([[makeQuery(id+"F43.imprint","IMPRINT",EDGE,{"derivedFrom":subQ0}),-1.0]])]})])],"isStart":true});}
            var Q2;
            {var subQ0=sQuery(id+"F47.wireOp",EDGE,"E94");Q2=makeQuery(id+"F47.imprint","IMPRINT",FACE,{"disambiguationData":[TD([[makeQuery(id+"F47.imprint","IMPRINT",EDGE,{"derivedFrom":subQ0}),-1.0]])]});}
            loft(context, id + "F57", {"operationType" : NewBodyOperationType.ADD, "sheetProfilesArray" : [{ "sheetProfileEntities" : qUnion([Q1]) }, { "sheetProfileEntities" : qUnion([Q2]) }]});
        }
        {
            var Q1;
            {var subQ0=sQuery(id+"F45.wireOp",EDGE,"E92");Q1=makeQuery(id+"F56.opLoft","CAP_FACE",FACE,{"disambiguationData":[OSD([makeQuery(id+"F45.imprint","IMPRINT",FACE,{"disambiguationData":[TD([[makeQuery(id+"F45.imprint","IMPRINT",EDGE,{"derivedFrom":subQ0}),-1.0]])]})])],"isStart":true});}
            var Q2;
            {var subQ0=sQuery(id+"F49.wireOp",EDGE,"E96");Q2=makeQuery(id+"F49.imprint","IMPRINT",FACE,{"disambiguationData":[TD([[makeQuery(id+"F49.imprint","IMPRINT",EDGE,{"derivedFrom":subQ0}),-1.0]])]});}
            loft(context, id + "F58", {"operationType" : NewBodyOperationType.ADD, "sheetProfilesArray" : [{ "sheetProfileEntities" : qUnion([Q1]) }, { "sheetProfileEntities" : qUnion([Q2]) }]});
        }
        {
            var Q1;
            {var subQ0=sQuery(id+"F47.wireOp",EDGE,"E94");Q1=makeQuery(id+"F57.opLoft","CAP_FACE",FACE,{"disambiguationData":[OSD([makeQuery(id+"F47.imprint","IMPRINT",FACE,{"disambiguationData":[TD([[makeQuery(id+"F47.imprint","IMPRINT",EDGE,{"derivedFrom":subQ0}),-1.0]])]})])],"isStart":true});}
            var Q2;
            {var subQ0=sQuery(id+"F51.wireOp",EDGE,"E98");Q2=makeQuery(id+"F51.imprint","IMPRINT",FACE,{"disambiguationData":[TD([[makeQuery(id+"F51.imprint","IMPRINT",EDGE,{"derivedFrom":subQ0}),-1.0]])]});}
            loft(context, id + "F59", {"operationType" : NewBodyOperationType.ADD, "sheetProfilesArray" : [{ "sheetProfileEntities" : qUnion([Q1]) }, { "sheetProfileEntities" : qUnion([Q2]) }]});
        }
        {
            var Q1;
            {var subQ0=sQuery(id+"F49.wireOp",EDGE,"E96");Q1=makeQuery(id+"F58.opLoft","CAP_FACE",FACE,{"disambiguationData":[OSD([makeQuery(id+"F49.imprint","IMPRINT",FACE,{"disambiguationData":[TD([[makeQuery(id+"F49.imprint","IMPRINT",EDGE,{"derivedFrom":subQ0}),-1.0]])]})])],"isStart":true});}
            var Q2;
            {var subQ0=sQuery(id+"F53.wireOp",EDGE,"E100");Q2=makeQuery(id+"F53.imprint","IMPRINT",FACE,{"disambiguationData":[TD([[makeQuery(id+"F53.imprint","IMPRINT",EDGE,{"derivedFrom":subQ0}),-1.0]])]});}
            loft(context, id + "F60", {"operationType" : NewBodyOperationType.ADD, "sheetProfilesArray" : [{ "sheetProfileEntities" : qUnion([Q1]) }, { "sheetProfileEntities" : qUnion([Q2]) }]});
        }
    });
